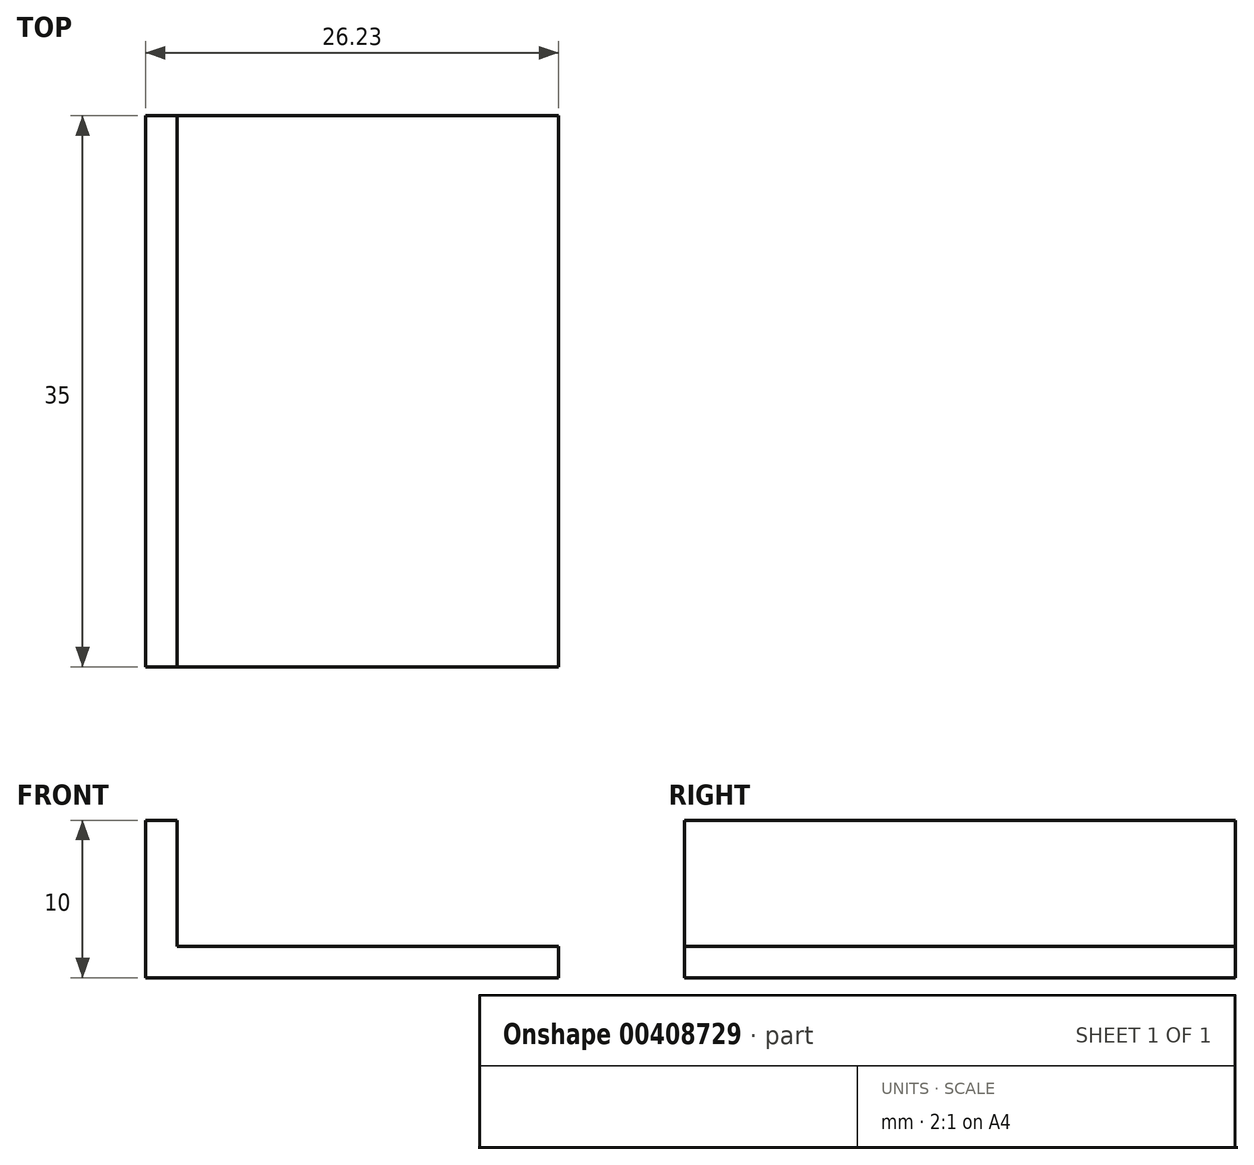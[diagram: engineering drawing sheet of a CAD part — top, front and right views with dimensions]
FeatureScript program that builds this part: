
annotation { "Feature Type Name" : "Feature", "Feature Type Description" : "" }
export const myFeature = defineFeature(function(context is Context, id is Id, definition is map)
    precondition{}
    {
        {
            var Q0;
            Q0=qCreatedBy(makeId("Top.planeOp"),FACE);
            var sketch = newSketch(context, id + "F0", { "sketchPlane" : qUnion([Q0])});
            skLineSegment(sketch, "E0.bottom", {"start": v(0, 0) * mm, "end": v(24.23, 0) * mm});
            skLineSegment(sketch, "E0.top", {"start": v(0, 35) * mm, "end": v(24.23, 35) * mm});
            skLineSegment(sketch, "E0.left", {"start": v(0, 0) * mm, "end": v(0, 35) * mm});
            skLineSegment(sketch, "E0.right", {"start": v(24.23, 0) * mm, "end": v(24.23, 35) * mm});
            skSolve(sketch);
        }
        {
            var Q0;
            Q0 = qSketchRegion(id + "F0", true);
            extrude(context, id + "F1", {"entities" : qUnion([Q0]), "depth" : 2 * mm});
        }
        {
            var Q0;
            Q0=makeQuery(id+"F1.opExtrude","SWEPT_FACE",FACE,{"disambiguationData":[OSD([sQuery(id+"F0.wireOp",EDGE,"E0.left")])]});
            var sketch = newSketch(context, id + "F2", { "sketchPlane" : qUnion([Q0])});
            skLineSegment(sketch, "E1", {"start": v(-35, 0) * mm, "end": v(-35, 10) * mm});
            skLineSegment(sketch, "E2", {"start": v(-35, 10) * mm, "end": v(0, 10) * mm});
            skLineSegment(sketch, "E3", {"start": v(0, 10) * mm, "end": v(0, 0) * mm});
            skLineSegment(sketch, "E4", {"start": v(0, 0) * mm, "end": v(-35, 0) * mm});
            skSolve(sketch);
        }
        {
            var Q0;
            Q0 = qSketchRegion(id + "F2", true);
            extrude(context, id + "F3", {"entities" : qUnion([Q0]), "operationType" : NewBodyOperationType.ADD, "depth" : 2 * mm});
        }
    });
